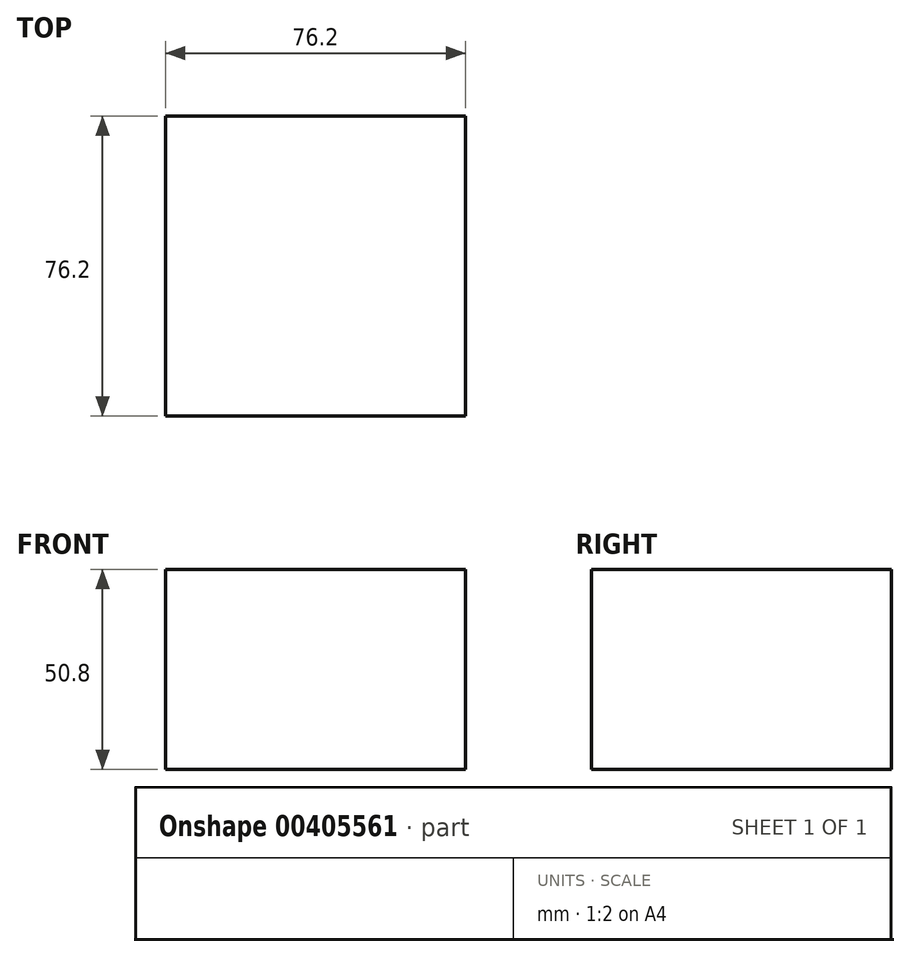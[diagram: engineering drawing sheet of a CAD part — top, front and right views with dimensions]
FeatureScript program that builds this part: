
annotation { "Feature Type Name" : "Feature", "Feature Type Description" : "" }
export const myFeature = defineFeature(function(context is Context, id is Id, definition is map)
    precondition{}
    {
        {
            var Q0;
            Q0=qCreatedBy(makeId("Top.planeOp"),FACE);
            var sketch = newSketch(context, id + "F0", { "sketchPlane" : qUnion([Q0])});
            skLineSegment(sketch, "E0", {"start": v(-38.1, 38.1) * mm, "end": v(38.1, 38.1) * mm});
            skLineSegment(sketch, "E1", {"start": v(38.1, 38.1) * mm, "end": v(38.1, -38.1) * mm});
            skLineSegment(sketch, "E2", {"start": v(38.1, -38.1) * mm, "end": v(-38.1, -38.1) * mm});
            skLineSegment(sketch, "E3", {"start": v(-38.1, -38.1) * mm, "end": v(-38.1, 38.1) * mm});
            skSolve(sketch);
        }
        {
            var Q0;
            Q0 = qSketchRegion(id + "F0", true);
            extrude(context, id + "F1", {"entities" : qUnion([Q0]), "depth" : 50.8 * mm});
        }
        {
            var Q0;
            Q0=makeQuery(id+"F1.opExtrude","CAP_FACE",FACE,{"disambiguationData":[OSD([sQuery(id+"F0.wireOp",EDGE,"E0"),sQuery(id+"F0.wireOp",EDGE,"E1"),sQuery(id+"F0.wireOp",EDGE,"E2"),sQuery(id+"F0.wireOp",EDGE,"E3")])],"isStart":false});
            var sketch = newSketch(context, id + "F2", { "sketchPlane" : qUnion([Q0])});
            skCircle(sketch, "E4", {"center": v(0, 0) * mm, "radius": 25.4 * mm});
            skSolve(sketch);
        }
        {
            var Q0;
            Q0=sQuery(id+"F2.wireOp",EDGE,"E4");
            extrude(context, id + "F3", {"bodyType" : ToolBodyType.SURFACE, "surfaceEntities" : qUnion([Q0]), "depth" : 25.4 * mm});
        }
    });
